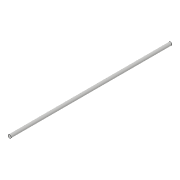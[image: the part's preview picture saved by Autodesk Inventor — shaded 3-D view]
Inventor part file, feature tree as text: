
AUTODESK INVENTOR PART (.ipt)
format: ipt  version: 2018.3 (Build 223284000, 284)  size: 69,120 bytes
history: native  units: in
note: dims shown in document units (in); Inventor stores cm internally (conversion verified against a paired STEP export)
features: extrude x1, sketch x1
ambient origin geometry x8: Origin, YZ Plane, XZ Plane, XY Plane, X Axis, Y Axis, Z Axis, Center Point
bodies: Solid1 (feature_tree)
feature tree (2):
  extrude  "Extrusion1"  Depth=6.5in TaperAngle=0.0deg
  sketch  "Sketch1"  dims[d0=0.125in d1=6.5in d2=0.0in]
